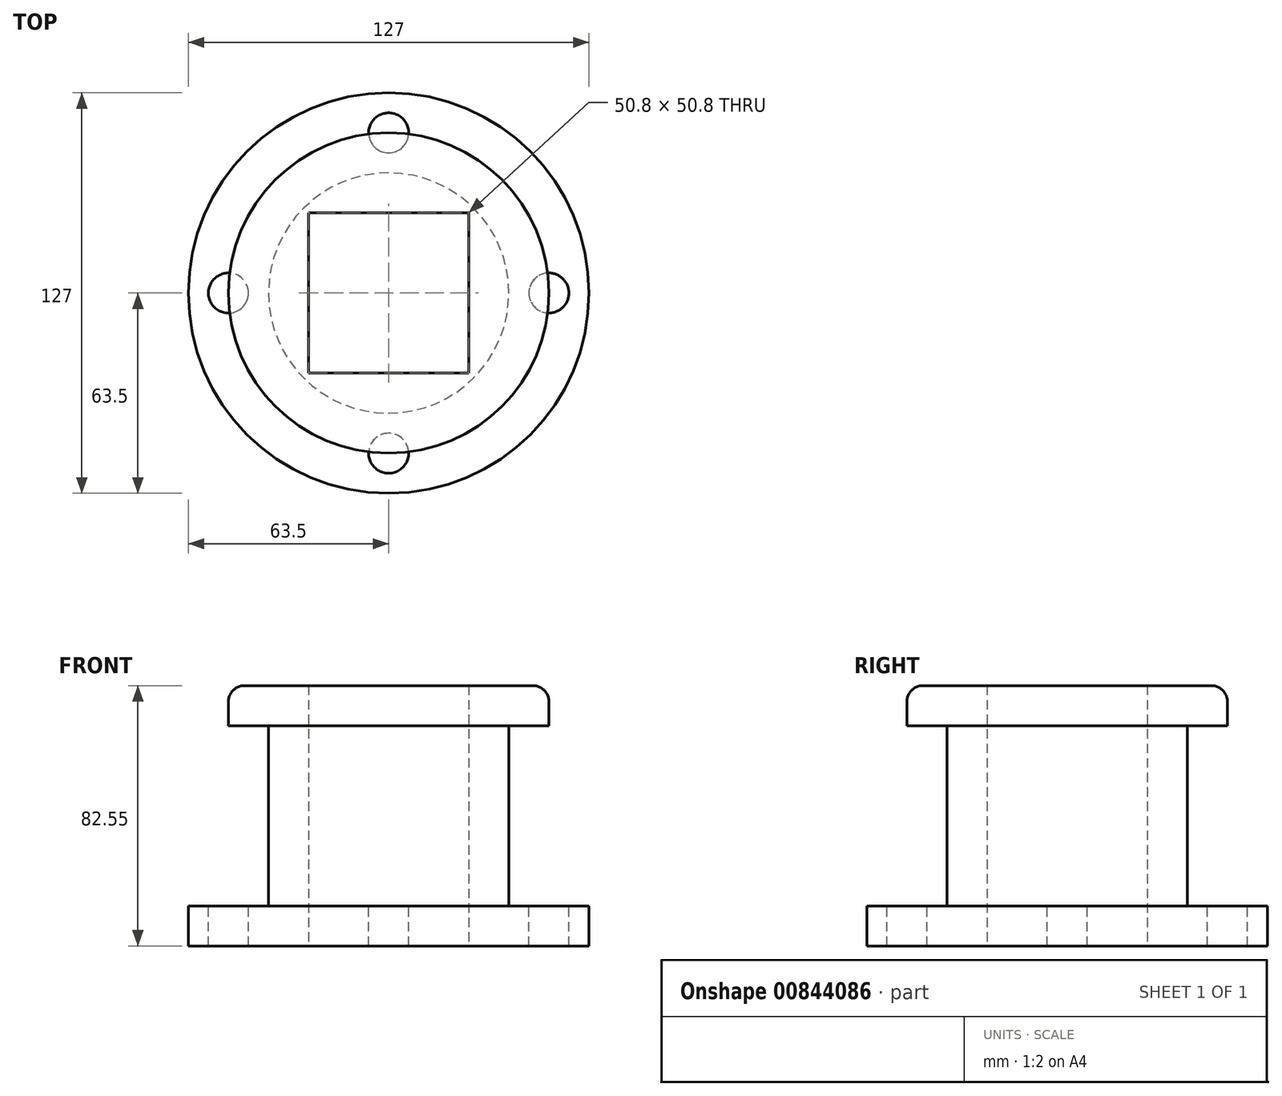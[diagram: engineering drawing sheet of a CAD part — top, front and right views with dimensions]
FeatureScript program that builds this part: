
annotation { "Feature Type Name" : "Feature", "Feature Type Description" : "" }
export const myFeature = defineFeature(function(context is Context, id is Id, definition is map)
    precondition{}
    {
        {
            var Q0;
            Q0=qCreatedBy(makeId("Top.planeOp"),FACE);
            var sketch = newSketch(context, id + "F0", { "sketchPlane" : qUnion([Q0])});
            skCircle(sketch, "E0", {"center": v(0, 0) * mm, "radius": 38.1 * mm});
            skSolve(sketch);
        }
        {
            var Q0;
            Q0 = qSketchRegion(id + "F0", true);
            extrude(context, id + "F1", {"entities" : qUnion([Q0]), "oppositeDirection" : true, "depth" : 57.15 * mm, "offsetDistance" : 25.4 * mm});
        }
        {
            var Q0;
            Q0=qCreatedBy(makeId("Top.planeOp"),FACE);
            var sketch = newSketch(context, id + "F2", { "sketchPlane" : qUnion([Q0])});
            skCircle(sketch, "E1", {"center": v(0, 0) * mm, "radius": 50.8 * mm});
            skSolve(sketch);
        }
        {
            var Q0;
            Q0 = qSketchRegion(id + "F2", true);
            extrude(context, id + "F3", {"entities" : qUnion([Q0]), "operationType" : NewBodyOperationType.ADD, "depth" : 12.7 * mm, "offsetDistance" : 25.4 * mm});
        }
        {
            var Q0;
            Q0=makeQuery(id+"F3.opExtrude","CAP_EDGE",EDGE,{"disambiguationData":[OSD([sQuery(id+"F2.wireOp",EDGE,"E1")])],"isStart":false});
            fillet(context, id + "F4", {"entities" : qUnion([Q0]), "radius" : 5.08 * mm, "tangentPropagation" : true, "allowEdgeOverflow" : false});
        }
        {
            var Q0;
            Q0=qCreatedBy(makeId("Top.planeOp"),FACE);
            var sketch = newSketch(context, id + "F5", { "sketchPlane" : qUnion([Q0])});
            skCircle(sketch, "E2", {"center": v(0, 0) * mm, "radius": 63.5 * mm});
            skSolve(sketch);
        }
        {
            var Q0;
            Q0 = qSketchRegion(id + "F5", true);
            extrude(context, id + "F6", {"entities" : qUnion([Q0]), "operationType" : NewBodyOperationType.ADD, "oppositeDirection" : true, "depth" : 69.85 * mm, "offsetDistance" : 25.4 * mm, "hasSecondDirection" : true, "secondDirectionOppositeDirection" : true, "secondDirectionDepth" : 57.15 * mm});
        }
        {
            var Q0;
            Q0=qCreatedBy(makeId("Top.planeOp"),FACE);
            var sketch = newSketch(context, id + "F7", { "sketchPlane" : qUnion([Q0])});
            skLineSegment(sketch, "E3.bottom", {"start": v(25.4, -25.4) * mm, "end": v(-25.4, -25.4) * mm});
            skLineSegment(sketch, "E3.top", {"start": v(25.4, 25.4) * mm, "end": v(-25.4, 25.4) * mm});
            skLineSegment(sketch, "E3.left", {"start": v(25.4, -25.4) * mm, "end": v(25.4, 25.4) * mm});
            skLineSegment(sketch, "E3.right", {"start": v(-25.4, -25.4) * mm, "end": v(-25.4, 25.4) * mm});
            skPoint(sketch, "E3.middle", {"position": v(0, 0) * mm});
            skSolve(sketch);
        }
        {
            var Q0;
            Q0 = qSketchRegion(id + "F7", true);
            extrude(context, id + "F8", {"entities" : qUnion([Q0]), "operationType" : NewBodyOperationType.REMOVE, "depth" : 25.4 * mm, "offsetDistance" : 25.4 * mm, "hasSecondDirection" : true, "secondDirectionOppositeDirection" : true, "secondDirectionDepth" : 109.73 * mm});
        }
        {
            var Q0;
            Q0=qCreatedBy(makeId("Top.planeOp"),FACE);
            var sketch = newSketch(context, id + "F9", { "sketchPlane" : qUnion([Q0])});
            skCircle(sketch, "E4", {"center": v(0, -50.8) * mm, "radius": 6.35 * mm});
            skCircle(sketch, "E5", {"center": v(-50.8, 0) * mm, "radius": 6.35 * mm});
            skCircle(sketch, "E6", {"center": v(50.8, 0) * mm, "radius": 6.35 * mm});
            skCircle(sketch, "E7", {"center": v(0, 50.8) * mm, "radius": 6.35 * mm});
            skSolve(sketch);
        }
        {
            var Q0;
            Q0 = qSketchRegion(id + "F9", true);
            extrude(context, id + "F10", {"entities" : qUnion([Q0]), "operationType" : NewBodyOperationType.REMOVE, "oppositeDirection" : true, "depth" : 103.89 * mm, "offsetDistance" : 25.4 * mm, "hasSecondDirection" : true, "secondDirectionOppositeDirection" : true, "secondDirectionDepth" : 38.35 * mm});
        }
    });
